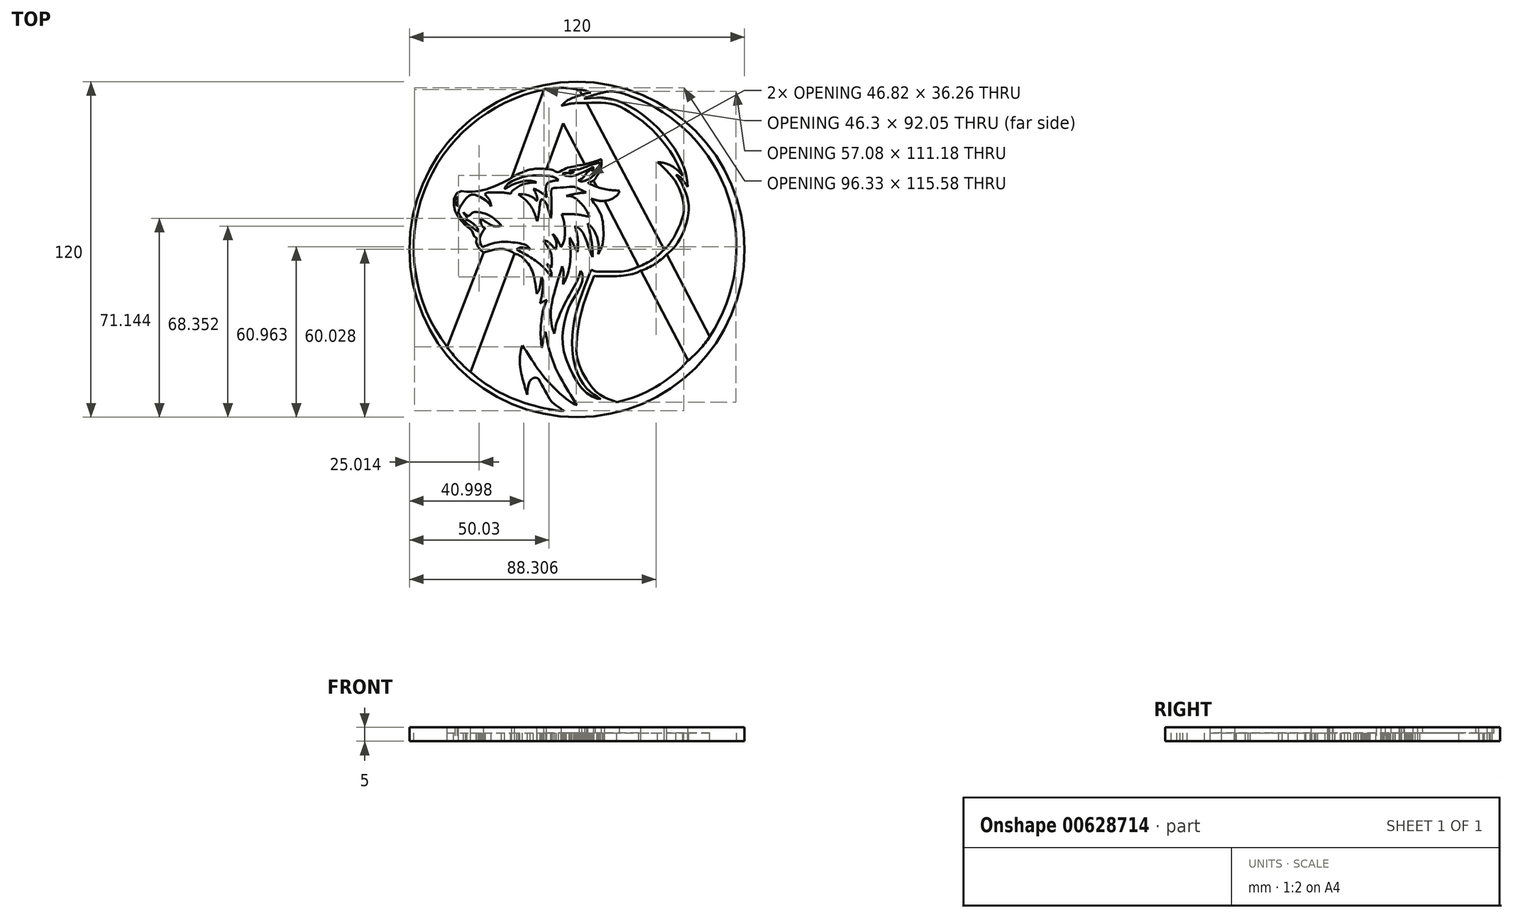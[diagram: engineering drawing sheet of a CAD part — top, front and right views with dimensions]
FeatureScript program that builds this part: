
annotation { "Feature Type Name" : "Feature", "Feature Type Description" : "" }
export const myFeature = defineFeature(function(context is Context, id is Id, definition is map)
    precondition{}
    {
        {
            var Q0;
            Q0=qCreatedBy(makeId("Top.planeOp"),FACE);
            var sketch = newSketch(context, id + "F0", { "sketchPlane" : qUnion([Q0])});
            skCircle(sketch, "E0", {"center": v(0, 0) * mm, "radius": 60 * mm});
            skLineSegment(sketch, "E1", {"start": v(0, 0) * mm, "end": v(60, 0) * mm});
            skSolve(sketch);
        }
        {
            var Q0;
            Q0 = qSketchRegion(id + "F0", true);
            extrude(context, id + "F1", {"entities" : qUnion([Q0]), "depth" : 5 * mm, "offsetDistance" : 25 * mm});
        }
        {
            var Q0;
            Q0=makeQuery(id+"F1.opExtrude","CAP_FACE",FACE,{"disambiguationData":[OSD([sQuery(id+"F0.wireOp",EDGE,"E0")])],"isStart":false});
            var sketch = newSketch(context, id + "F2", { "sketchPlane" : qUnion([Q0])});
            skLineSegment(sketch, "E2", {"start": v(-46.49, -34.88) * mm, "end": v(-33.38, -1.05) * mm});
            skFitSpline(sketch, "E3", {"points": [v(-33.38, -1.05) * mm, v(-34.17, -0.52) * mm, v(-35.37, 0.87) * mm, v(-36.07, 2.59) * mm, v(-35.97, 4.21) * mm, v(-36.9, 4.86) * mm, v(-37.83, 7.18) * mm, v(-38.3, 7.46) * mm, v(-40.7, 9.4) * mm, v(-42.79, 12.05) * mm, v(-43.86, 14.6) * mm, v(-44.04, 17.94) * mm, v(-42.51, 20.62) * mm, v(-40.29, 20.72) * mm, v(-37.46, 20.62) * mm, v(-32.91, 21.37) * mm, v(-26.4, 23.96) * mm, v(-23.59, 25.51) * mm, v(-23.4, 25.77) * mm], "startDerivative": vector(-21.56, 12.24) * mm, "endDerivative": vector(5.42, 11.23) * mm});
            skLineSegment(sketch, "E4", {"start": v(-23.4, 25.77) * mm, "end": v(-11.84, 57.17) * mm});
            skArc(sketch, "E5", {"start": v(-11.84, 57.17) * mm, "mid": v(-54.75, 20.77) * mm, "end": v(-46.49, -34.88) * mm});
            skLineSegment(sketch, "E6", {"start": v(-10.87, 28.8) * mm, "end": v(-4.96, 45.18) * mm});
            skLineSegment(sketch, "E7", {"start": v(-4.96, 45.18) * mm, "end": v(2.82, 30.48) * mm});
            skFitSpline(sketch, "E8", {"points": [v(2.82, 30.48) * mm, v(-0.57, 29.84) * mm, v(-4.3, 28.83) * mm, v(-6.98, 27.68) * mm, v(-8.34, 28.31) * mm, v(-10.87, 28.8) * mm], "startDerivative": vector(-14.97, -2.9) * mm, "endDerivative": vector(-14.54, 1.3) * mm});
            skLineSegment(sketch, "E9", {"start": v(0.84, 57.1) * mm, "end": v(1.79, 55.35) * mm});
            skFitSpline(sketch, "E10", {"points": [v(1.79, 55.35) * mm, v(2.86, 55.77) * mm, v(4.94, 56.14) * mm], "startDerivative": vector(2.3, 1.07) * mm, "endDerivative": vector(3.92, 0.54) * mm});
            skFitSpline(sketch, "E11", {"points": [v(4.94, 56.14) * mm, v(2.72, 56.93) * mm, v(0.84, 57.1) * mm], "startDerivative": vector(-4.26, 1.8) * mm, "endDerivative": vector(-3.93, 0.1) * mm});
            skLineSegment(sketch, "E12", {"start": v(-38.15, -43.82) * mm, "end": v(-22.3, -1.52) * mm});
            skFitSpline(sketch, "E13", {"points": [v(-22.3, -1.52) * mm, v(-20.22, -2.35) * mm, v(-18, -4.48) * mm, v(-16.37, -6.87) * mm, v(-15.08, -11.26) * mm, v(-14.4, -15.69) * mm, v(-14.4, -15.87) * mm], "startDerivative": vector(13.58, -3.84) * mm, "endDerivative": vector(0, -2.59) * mm});
            skFitSpline(sketch, "E14", {"points": [v(-14.4, -15.87) * mm, v(-13.67, -14.7) * mm, v(-13.09, -12.52) * mm, v(-12.7, -9.86) * mm], "startDerivative": vector(2.88, 3.88) * mm, "endDerivative": vector(0.92, 7.04) * mm});
            skFitSpline(sketch, "E15", {"points": [v(-12.7, -9.86) * mm, v(-12.2, -11.16) * mm, v(-12.39, -15.28) * mm, v(-13.2, -19.27) * mm], "startDerivative": vector(2.62, -4.79) * mm, "endDerivative": vector(-2.31, -9.85) * mm});
            skFitSpline(sketch, "E16", {"points": [v(-13.2, -19.27) * mm, v(-12.2, -18.7) * mm, v(-10.79, -18.09) * mm], "startDerivative": vector(2.05, 1.23) * mm, "endDerivative": vector(2.75, 1.13) * mm});
            skFitSpline(sketch, "E17", {"points": [v(-10.79, -18.09) * mm, v(-11.98, -21.3) * mm, v(-12.7, -25.28) * mm, v(-13.04, -30.32) * mm, v(-12.6, -35.24) * mm], "startDerivative": vector(-5.92, -14.1) * mm, "endDerivative": vector(2.31, -18.23) * mm});
            skFitSpline(sketch, "E18", {"points": [v(-12.6, -35.24) * mm, v(-11.92, -31.87) * mm, v(-11.18, -29.5) * mm], "startDerivative": vector(1.15, 6.53) * mm, "endDerivative": vector(1.7, 4.92) * mm});
            skFitSpline(sketch, "E19", {"points": [v(-11.18, -29.5) * mm, v(-10.32, -34.2) * mm, v(-9.13, -38.45) * mm, v(-7.5, -42.78) * mm, v(-4.05, -49.14) * mm, v(0, -55.7) * mm], "startDerivative": vector(4.16, -25.97) * mm, "endDerivative": vector(17.44, -27.8) * mm});
            skFitSpline(sketch, "E20", {"points": [v(0, -55.7) * mm, v(-2.24, -54.63) * mm, v(-6.84, -50.89) * mm, v(-12.8, -44.36) * mm, v(-16.52, -38.89) * mm, v(-19.53, -34.4) * mm], "startDerivative": vector(-15.9, 6.3) * mm, "endDerivative": vector(-15.34, 22.51) * mm});
            skFitSpline(sketch, "E21", {"points": [v(-19.53, -34.4) * mm, v(-20.18, -36.36) * mm, v(-20.45, -41.1) * mm, v(-19.79, -45.08) * mm, v(-18.66, -49.13) * mm, v(-17.8, -52.06) * mm], "startDerivative": vector(-4.69, -11.1) * mm, "endDerivative": vector(4.51, -15) * mm});
            skFitSpline(sketch, "E22", {"points": [v(-17.8, -52.06) * mm, v(-17.61, -49.34) * mm, v(-16.89, -47.25) * mm, v(-15.77, -46.14) * mm, v(-14.8, -45.9) * mm, v(-14, -46.11) * mm, v(-12.82, -48.04) * mm, v(-10.65, -51.85) * mm, v(-8.9, -54.58) * mm, v(-4.64, -57.76) * mm, v(-4.64, -57.76) * mm], "startDerivative": vector(0.44, 23.71) * mm, "endDerivative": vector(-0.04, -0.37) * mm});
            skFitSpline(sketch, "E23", {"points": [v(-4.64, -57.76) * mm, v(-6.58, -57.76) * mm, v(-9.98, -57.16) * mm, v(-15.93, -55.78) * mm, v(-23.66, -53.1) * mm, v(-26.4, -51.82) * mm, v(-32.93, -47.92) * mm, v(-38.15, -43.82) * mm], "startDerivative": vector(-20.53, -1.09) * mm, "endDerivative": vector(-28.95, 24.63) * mm});
            skFitSpline(sketch, "E24", {"points": [v(1.34, -7.66) * mm, v(1.89, -8.56) * mm, v(1.98, -10.4) * mm, v(1.29, -13.28) * mm, v(-1.4, -17.85) * mm, v(-3.38, -22.03) * mm, v(-4.93, -28.7) * mm, v(-4.83, -35.75) * mm, v(-1.91, -43.87) * mm, v(2.1, -50.06) * mm, v(6.63, -53.19) * mm, v(8.56, -53.57) * mm], "startDerivative": vector(14.5, -18.02) * mm, "endDerivative": vector(28.92, -2.36) * mm});
            skFitSpline(sketch, "E25", {"points": [v(8.56, -53.57) * mm, v(6.73, -52.4) * mm, v(4.6, -50.75) * mm, v(2.55, -48.53) * mm, v(0.37, -44.86) * mm, v(-0.72, -41.8) * mm, v(-1.7, -35.87) * mm, v(-1.52, -29.5) * mm, v(-0.5, -23.24) * mm, v(1.28, -17.24) * mm, v(3.74, -10.65) * mm, v(5.12, -7.31) * mm, v(5.12, -7.31) * mm], "startDerivative": vector(-28.43, 17.64) * mm, "endDerivative": vector(0.41, 0.2) * mm});
            skFitSpline(sketch, "E26", {"points": [v(5.12, -7.31) * mm, v(7.08, -7.87) * mm, v(12.4, -7.96) * mm, v(17.2, -7.75) * mm, v(22.17, -6.17) * mm], "startDerivative": vector(9.64, -3.8) * mm, "endDerivative": vector(18.04, 7.02) * mm});
            skLineSegment(sketch, "E27", {"start": v(22.17, -6.17) * mm, "end": v(9.86, 17.38) * mm});
            skFitSpline(sketch, "E28", {"points": [v(9.86, 17.38) * mm, v(8.16, 17.38) * mm, v(5.05, 18.15) * mm], "startDerivative": vector(-3.75, -0.28) * mm, "endDerivative": vector(-5.77, 1.7) * mm});
            skFitSpline(sketch, "E29", {"points": [v(5.05, 18.15) * mm, v(5.63, 17.24) * mm, v(8.02, 13.66) * mm, v(9.13, 10.5) * mm, v(9.47, 6.96) * mm, v(9.14, 1.8) * mm, v(7.6, -1.65) * mm], "startDerivative": vector(4.69, -7.98) * mm, "endDerivative": vector(-10.37, -17.94) * mm});
            skFitSpline(sketch, "E30", {"points": [v(7.6, -1.65) * mm, v(7.8, 0.11) * mm, v(7.49, 3.13) * mm, v(6.25, 6.49) * mm, v(4.82, 8.42) * mm, v(3.82, 9.31) * mm], "startDerivative": vector(1.7, 9.49) * mm, "endDerivative": vector(-6.48, 5.26) * mm});
            skFitSpline(sketch, "E31", {"points": [v(3.82, 9.31) * mm, v(4.27, 7.86) * mm, v(5.16, 3.44) * mm, v(5.6, -0.82) * mm, v(5.55, -2.7) * mm], "startDerivative": vector(2.36, -6.84) * mm, "endDerivative": vector(-0.55, -8.47) * mm});
            skFitSpline(sketch, "E32", {"points": [v(5.55, -2.7) * mm, v(4.58, -0.32) * mm, v(3.43, 3) * mm, v(2, 6.15) * mm, v(0.4, 7.82) * mm, v(-0.65, 8.4) * mm], "startDerivative": vector(-4.82, 11.32) * mm, "endDerivative": vector(-7.3, 3.5) * mm});
            skFitSpline(sketch, "E33", {"points": [v(-0.65, 8.4) * mm, v(-0.19, 6.31) * mm, v(0.34, 3.16) * mm, v(0.3, 0.22) * mm, v(0.15, -1) * mm], "startDerivative": vector(1.83, -8.24) * mm, "endDerivative": vector(-0.92, -5.9) * mm});
            skFitSpline(sketch, "E34", {"points": [v(0.15, -1) * mm, v(-0.5, 0.18) * mm, v(-1.47, 2.17) * mm, v(-2.6, 4.28) * mm], "startDerivative": vector(-2.33, 3.92) * mm, "endDerivative": vector(-3.13, 5.64) * mm});
            skFitSpline(sketch, "E35", {"points": [v(-2.6, 4.28) * mm, v(-2.46, 1.79) * mm, v(-2.34, -3.15) * mm, v(-3.46, -9.06) * mm, v(-4.97, -12.54) * mm], "startDerivative": vector(0.59, -11.93) * mm, "endDerivative": vector(-6.71, -13.43) * mm});
            skFitSpline(sketch, "E36", {"points": [v(-4.97, -12.54) * mm, v(-4.83, -10.25) * mm, v(-4.83, -8) * mm, v(-5.3, -6.02) * mm], "startDerivative": vector(0.43, 6.67) * mm, "endDerivative": vector(-1.83, 6) * mm});
            skFitSpline(sketch, "E37", {"points": [v(-5.3, -6.02) * mm, v(-5.97, -8.23) * mm, v(-7.65, -13.86) * mm, v(-8.87, -18.65) * mm, v(-9.38, -22.52) * mm, v(-9.11, -26.8) * mm, v(-8.1, -30.2) * mm], "startDerivative": vector(-4.59, -15.27) * mm, "endDerivative": vector(7.54, -20.96) * mm});
            skFitSpline(sketch, "E38", {"points": [v(-8.1, -30.2) * mm, v(-7.43, -26.81) * mm, v(-5.58, -21.9) * mm, v(-2.94, -16.7) * mm, v(-0.85, -13.01) * mm, v(0.66, -9.79) * mm, v(1.34, -7.66) * mm], "startDerivative": vector(3.24, 21.07) * mm, "endDerivative": vector(4.62, 16.25) * mm});
            skFitSpline(sketch, "E39", {"points": [v(31.26, 0) * mm, v(34.04, 3.29) * mm, v(37.22, 9.75) * mm, v(38.22, 15.62) * mm, v(36.23, 22.58) * mm, v(32.65, 27.65) * mm, v(28.87, 31.18) * mm], "startDerivative": vector(19.68, 20.28) * mm, "endDerivative": vector(-24.78, 21.54) * mm});
            skFitSpline(sketch, "E40", {"points": [v(28.87, 31.18) * mm, v(30.68, 31.05) * mm, v(33.64, 29.98) * mm, v(36.21, 28.16) * mm, v(37.87, 26.33) * mm], "startDerivative": vector(8.16, 0.03) * mm, "endDerivative": vector(6.3, -7.66) * mm});
            skFitSpline(sketch, "E41", {"points": [v(37.87, 26.33) * mm, v(34.98, 32.47) * mm, v(27.72, 42.09) * mm, v(21.1, 47.56) * mm, v(14.87, 51.28) * mm, v(9.32, 52.5) * mm, v(3.38, 52.38) * mm], "startDerivative": vector(-14.7, 36.43) * mm, "endDerivative": vector(-40.77, -2.44) * mm});
            skLineSegment(sketch, "E42", {"start": v(3.38, 52.38) * mm, "end": v(31.26, 0) * mm});
            skFitSpline(sketch, "E43", {"points": [v(32.1, -1.72) * mm, v(34.65, 0.58) * mm, v(37.67, 5.34) * mm, v(39.86, 12.73) * mm, v(39.47, 18.64) * mm, v(36.77, 24.9) * mm, v(35.4, 26.72) * mm], "startDerivative": vector(18.8, 15.01) * mm, "endDerivative": vector(-11.44, 13.12) * mm});
            skFitSpline(sketch, "E44", {"points": [v(35.4, 26.72) * mm, v(37.01, 25.85) * mm, v(39.58, 22.4) * mm], "startDerivative": vector(4.06, -1.53) * mm, "endDerivative": vector(4.3, -6.75) * mm});
            skFitSpline(sketch, "E45", {"points": [v(39.58, 22.4) * mm, v(39.16, 26.48) * mm, v(36.77, 32.91) * mm, v(31.7, 40.47) * mm, v(26.42, 45.83) * mm, v(18.62, 51.34) * mm, v(10.27, 54.23) * mm, v(2.54, 53.88) * mm], "startDerivative": vector(-1.66, 37) * mm, "endDerivative": vector(-53.18, -6.81) * mm});
            skFitSpline(sketch, "E46", {"points": [v(2.54, 53.88) * mm, v(4.93, 54.92) * mm, v(9.15, 56.12) * mm], "startDerivative": vector(5.07, 2.46) * mm, "endDerivative": vector(8.02, 2.04) * mm});
            skFitSpline(sketch, "E47", {"points": [v(9.15, 56.12) * mm, v(11.4, 56.52) * mm, v(14.67, 56.3) * mm, v(18.96, 54.98) * mm], "startDerivative": vector(7.73, 1.8) * mm, "endDerivative": vector(11.22, -4) * mm});
            skArc(sketch, "E48", {"start": v(47.53, -31.22) * mm, "mid": v(54.17, 18.81) * mm, "end": v(18.96, 54.98) * mm});
            skLineSegment(sketch, "E49", {"start": v(47.53, -31.22) * mm, "end": v(32.1, -1.72) * mm});
            skLineSegment(sketch, "E50", {"start": v(22.84, -7.6) * mm, "end": v(39.82, -39.7) * mm});
            skFitSpline(sketch, "E51", {"points": [v(22.84, -7.6) * mm, v(19.85, -8.8) * mm, v(12.97, -9.6) * mm, v(6.1, -9.5) * mm], "startDerivative": vector(-10.27, -5.18) * mm, "endDerivative": vector(-17.93, 0.7) * mm});
            skFitSpline(sketch, "E52", {"points": [v(6.1, -9.5) * mm, v(4, -14.83) * mm, v(1.2, -23.88) * mm, v(0, -31.84) * mm, v(0.46, -40.49) * mm, v(6.73, -50.75) * mm, v(10.57, -53.2) * mm, v(14.3, -54.63) * mm], "startDerivative": vector(-15.99, -38.63) * mm, "endDerivative": vector(35.93, -13.2) * mm});
            skArc(sketch, "E53", {"start": v(14.3, -54.63) * mm, "mid": v(28.24, -49.2) * mm, "end": v(39.82, -39.7) * mm});
            skFitSpline(sketch, "E54", {"points": [v(-9.2, -9.78) * mm, v(-13.22, -5.25) * mm, v(-21.57, 0) * mm], "startDerivative": vector(-7.9, 10.5) * mm, "endDerivative": vector(-16.5, 9.1) * mm});
            skFitSpline(sketch, "E55", {"points": [v(-21.57, 0) * mm, v(-20.13, 0.71) * mm, v(-16.7, 0) * mm], "startDerivative": vector(3.13, 2.36) * mm, "endDerivative": vector(6.4, -2.08) * mm});
            skFitSpline(sketch, "E56", {"points": [v(-16.7, 0) * mm, v(-18.44, 1.6) * mm, v(-23.11, 2.55) * mm, v(-27.94, 2.65) * mm, v(-33.9, 0.86) * mm], "startDerivative": vector(-7.61, 9.84) * mm, "endDerivative": vector(-20.74, -7.72) * mm});
            skFitSpline(sketch, "E57", {"points": [v(-33.9, 0.86) * mm, v(-34.8, 3.5) * mm, v(-33.9, 6.13) * mm, v(-32.8, 7.67) * mm], "startDerivative": vector(-3.8, 7.28) * mm, "endDerivative": vector(3.74, 4.76) * mm});
            skFitSpline(sketch, "E58", {"points": [v(-32.8, 7.67) * mm, v(-33.9, 8.32) * mm, v(-34.4, 9.76) * mm, v(-34.45, 11.15) * mm], "startDerivative": vector(-3.87, 1.5) * mm, "endDerivative": vector(0.05, 4.05) * mm});
            skFitSpline(sketch, "E59", {"points": [v(-34.45, 11.15) * mm, v(-32.8, 9.96) * mm, v(-30.67, 8.72) * mm, v(-29.33, 8.27) * mm, v(-27, 8.47) * mm], "startDerivative": vector(6.14, -4.73) * mm, "endDerivative": vector(9.51, 1.44) * mm});
            skFitSpline(sketch, "E60", {"points": [v(-27, 8.47) * mm, v(-28.78, 10.3) * mm, v(-32.26, 12.6) * mm, v(-35.24, 13.34) * mm, v(-37.13, 13.3) * mm, v(-38.38, 12.25) * mm, v(-39.17, 12.1) * mm, v(-40.66, 13.24) * mm], "startDerivative": vector(-10.12, 11.46) * mm, "endDerivative": vector(-11.9, 11.25) * mm});
            skFitSpline(sketch, "E61", {"points": [v(-40.66, 13.24) * mm, v(-39.9, 12.1) * mm, v(-39.4, 11.47) * mm, v(-39.88, 10.7) * mm], "startDerivative": vector(1.84, -3.2) * mm, "endDerivative": vector(-2.34, -2.57) * mm});
            skFitSpline(sketch, "E62", {"points": [v(-39.88, 10.7) * mm, v(-38.96, 10.38) * mm, v(-36.86, 9) * mm, v(-35.66, 7.67) * mm, v(-35.26, 6.46) * mm], "startDerivative": vector(4.18, -1.1) * mm, "endDerivative": vector(1.3, -5.52) * mm});
            skFitSpline(sketch, "E63", {"points": [v(-35.26, 6.46) * mm, v(-36.84, 7.39) * mm, v(-39.17, 9.13) * mm, v(-41.4, 11.45) * mm, v(-42.44, 13.5) * mm, v(-41.53, 15.61) * mm, v(-39.88, 18.04) * mm, v(-38.3, 19.4) * mm, v(-36.6, 19.57) * mm, v(-34.45, 18.7) * mm, v(-32.44, 17.44) * mm, v(-31.25, 16.14) * mm, v(-30.76, 15.44) * mm], "startDerivative": vector(-19.73, 11.03) * mm, "endDerivative": vector(8.3, -12.4) * mm});
            skFitSpline(sketch, "E64", {"points": [v(-30.76, 15.44) * mm, v(-30.9, 16.58) * mm, v(-31.75, 18.3) * mm, v(-32.97, 19.7) * mm], "startDerivative": vector(-0.17, 3.87) * mm, "endDerivative": vector(-3.6, 3.66) * mm});
            skFitSpline(sketch, "E65", {"points": [v(-32.97, 19.7) * mm, v(-32.37, 20.2) * mm, v(-29.75, 20.44) * mm, v(-26.51, 20.38) * mm, v(-23.76, 19.94) * mm], "startDerivative": vector(3.07, 3.83) * mm, "endDerivative": vector(9.66, -1.93) * mm});
            skFitSpline(sketch, "E66", {"points": [v(-23.76, 19.94) * mm, v(-23.27, 20.89) * mm, v(-21.35, 22.27) * mm, v(-18.44, 23.57) * mm, v(-14.49, 24) * mm, v(-14.49, 24) * mm], "startDerivative": vector(2.02, 5.85) * mm, "endDerivative": vector(-0.05, 0.18) * mm});
            skFitSpline(sketch, "E67", {"points": [v(-14.49, 24) * mm, v(-15.49, 24.42) * mm, v(-18.83, 24.46) * mm, v(-22.88, 23.24) * mm, v(-24.92, 22.1) * mm, v(-25.75, 21.62) * mm, v(-25.83, 22) * mm, v(-24.8, 23.33) * mm, v(-21.25, 25.34) * mm, v(-16.25, 26.47) * mm, v(-12.37, 26.44) * mm, v(-9.95, 26.34) * mm, v(-7.83, 25.73) * mm, v(-6.54, 24.78) * mm], "startDerivative": vector(-16.04, 8.88) * mm, "endDerivative": vector(18.42, -16.07) * mm});
            skFitSpline(sketch, "E68", {"points": [v(-6.54, 24.78) * mm, v(-8.55, 24.53) * mm, v(-10.46, 23.76) * mm, v(-11.14, 21.91) * mm, v(-10.77, 18.59) * mm], "startDerivative": vector(-8.44, -0.8) * mm, "endDerivative": vector(2.08, -11.65) * mm});
            skFitSpline(sketch, "E69", {"points": [v(-10.77, 18.59) * mm, v(-12.34, 20.06) * mm, v(-14.83, 21.46) * mm, v(-15.63, 21.7) * mm], "startDerivative": vector(-3.74, 4.08) * mm, "endDerivative": vector(-3, 0.69) * mm});
            skFitSpline(sketch, "E70", {"points": [v(-15.63, 21.7) * mm, v(-14.84, 20.25) * mm, v(-14.22, 18.59) * mm, v(-14.37, 17.45) * mm, v(-15.5, 18.38) * mm, v(-17.57, 19.45) * mm, v(-19.36, 19.78) * mm, v(-20.96, 19.7) * mm], "startDerivative": vector(5.6, -10.11) * mm, "endDerivative": vector(-11.36, -1.2) * mm});
            skFitSpline(sketch, "E71", {"points": [v(-20.96, 19.7) * mm, v(-19.45, 18.59) * mm, v(-17.17, 16.39) * mm, v(-15.38, 13.42) * mm, v(-14.27, 10.16) * mm], "startDerivative": vector(7.17, -5) * mm, "endDerivative": vector(3.61, -12.23) * mm});
            skFitSpline(sketch, "E72", {"points": [v(-14.27, 10.16) * mm, v(-13.9, 11.58) * mm, v(-13.41, 14.9) * mm, v(-13.14, 16.87) * mm, v(-12.67, 17.94) * mm, v(-11.45, 17.12) * mm, v(-9.96, 13.54) * mm, v(-9.45, 11.26) * mm], "startDerivative": vector(3.19, 10.27) * mm, "endDerivative": vector(2.68, -13.95) * mm});
            skFitSpline(sketch, "E73", {"points": [v(-9.45, 11.26) * mm, v(-9.11, 12.82) * mm, v(-9.14, 16.76) * mm, v(-9.21, 20.81) * mm, v(-8.95, 21.72) * mm, v(-6.5, 22.1) * mm, v(-2.65, 22.38) * mm, v(-1.01, 22.38) * mm, v(3.3, 20.38) * mm], "startDerivative": vector(4.25, 14.55) * mm, "endDerivative": vector(29.84, -16) * mm});
            skFitSpline(sketch, "E74", {"points": [v(3.3, 20.38) * mm, v(1.3, 20.2) * mm, v(-1.65, 19.7) * mm, v(-3.78, 19.12) * mm], "startDerivative": vector(-6.15, -0.37) * mm, "endDerivative": vector(-6.25, -1.83) * mm});
            skFitSpline(sketch, "E75", {"points": [v(-3.78, 19.12) * mm, v(-1.49, 18.83) * mm, v(1.57, 16.38) * mm, v(3.64, 13.54) * mm, v(4.4, 11.66) * mm], "startDerivative": vector(10.1, 0.22) * mm, "endDerivative": vector(2.98, -8.67) * mm});
            skFitSpline(sketch, "E76", {"points": [v(4.4, 11.66) * mm, v(1.58, 12.27) * mm, v(-2.02, 12.66) * mm, v(-5.48, 12.6) * mm], "startDerivative": vector(-8.75, 2.07) * mm, "endDerivative": vector(-10.03, -0.47) * mm});
            skFitSpline(sketch, "E77", {"points": [v(-5.48, 12.6) * mm, v(-4.63, 9.7) * mm, v(-4.48, 3.8) * mm, v(-5.66, 0.84) * mm], "startDerivative": vector(3.24, -8.58) * mm, "endDerivative": vector(-4.79, -8.48) * mm});
            skFitSpline(sketch, "E78", {"points": [v(-9.2, -9.78) * mm, v(-9.07, -9.08) * mm, v(-9.6, -7.2) * mm, v(-10.77, -5.3) * mm], "startDerivative": vector(0.85, 2.7) * mm, "endDerivative": vector(-3.21, 4.5) * mm});
            skFitSpline(sketch, "E79", {"points": [v(-10.77, -5.3) * mm, v(-10.36, -5.42) * mm, v(-9.57, -6) * mm, v(-9.2, -6.52) * mm], "startDerivative": vector(1.39, -0.23) * mm, "endDerivative": vector(0.93, -1.53) * mm});
            skFitSpline(sketch, "E80", {"points": [v(-9.2, -6.52) * mm, v(-8.98, -4.53) * mm, v(-9.36, -1.17) * mm, v(-10.58, 1.13) * mm, v(-12.04, 3.13) * mm], "startDerivative": vector(1.31, 8.28) * mm, "endDerivative": vector(-6.08, 8.16) * mm});
            skFitSpline(sketch, "E81", {"points": [v(-12.04, 3.13) * mm, v(-10.63, 2.89) * mm, v(-8.77, 1.2) * mm, v(-7.54, 0) * mm], "startDerivative": vector(4.75, 0.01) * mm, "endDerivative": vector(3.6, -3.35) * mm});
            skFitSpline(sketch, "E82", {"points": [v(-7.54, 0) * mm, v(-7.36, 1.92) * mm, v(-7.7, 3.57) * mm, v(-8.73, 5.5) * mm], "startDerivative": vector(0.85, 5.9) * mm, "endDerivative": vector(-3.33, 5.51) * mm});
            skFitSpline(sketch, "E83", {"points": [v(-8.73, 5.5) * mm, v(-7.73, 4.57) * mm, v(-6.54, 2.59) * mm, v(-5.66, 0.84) * mm], "startDerivative": vector(3.53, -2.76) * mm, "endDerivative": vector(2.4, -4.9) * mm});
            skFitSpline(sketch, "E84", {"points": [v(0.44, 24.78) * mm, v(1.35, 24.32) * mm, v(3.56, 24.89) * mm, v(5.95, 26.42) * mm, v(7.67, 28.88) * mm, v(8.13, 30.34) * mm, v(8.15, 31.22) * mm], "startDerivative": vector(6.33, -4.98) * mm, "endDerivative": vector(-0.25, 7.3) * mm});
            skFitSpline(sketch, "E85", {"points": [v(8.15, 31.22) * mm, v(6.62, 30.73) * mm, v(3.57, 29.7) * mm, v(0.7, 28.72) * mm, v(-1.16, 28.4) * mm, v(-2.77, 28.17) * mm], "startDerivative": vector(-8.2, -2.6) * mm, "endDerivative": vector(-9.34, -1.47) * mm});
            skFitSpline(sketch, "E86", {"points": [v(-2.77, 28.17) * mm, v(-2.48, 27.95) * mm, v(-1.59, 27.93) * mm, v(-1.1, 27.8) * mm], "startDerivative": vector(0.8, -1.02) * mm, "endDerivative": vector(1.31, -0.58) * mm});
            skFitSpline(sketch, "E87", {"points": [v(-1.1, 27.8) * mm, v(-1.53, 27.4) * mm, v(-3.11, 27.34) * mm, v(-4.44, 27.4) * mm, v(-5.22, 27.1) * mm], "startDerivative": vector(-1.7, -2.48) * mm, "endDerivative": vector(-3.3, -1.65) * mm});
            skFitSpline(sketch, "E88", {"points": [v(-5.22, 27.1) * mm, v(-4.72, 26.64) * mm, v(-2.77, 26.26) * mm, v(-0.34, 26.6) * mm, v(2.1, 27.68) * mm, v(4.6, 28.8) * mm, v(5.75, 29.54) * mm, v(5.93, 29.1) * mm, v(5.6, 28.17) * mm, v(5.3, 28.37) * mm, v(5.2, 28.6) * mm, v(4.4, 28.26) * mm, v(3.48, 27.36) * mm, v(2.44, 26.04) * mm, v(1.4, 25.13) * mm, v(0.44, 24.78) * mm], "startDerivative": vector(7.66, -9.88) * mm, "endDerivative": vector(-16, -4.19) * mm});
            skFitSpline(sketch, "E89", {"points": [v(-42.53, 15.94) * mm, v(-42.87, 17.53) * mm, v(-42.8, 18.79) * mm, v(-43.46, 18.11) * mm, v(-43.6, 16.99) * mm, v(-43.27, 16.14) * mm, v(-42.56, 15.58) * mm, v(-42.53, 15.94) * mm]});
            skSolve(sketch);
        }
        {
            var Q0;
            Q0 = qSketchRegion(id + "F2", true);
            extrude(context, id + "F3", {"entities" : qUnion([Q0]), "operationType" : NewBodyOperationType.REMOVE, "endBound" : BoundingType.THROUGH_ALL, "oppositeDirection" : true, "depth" : 25 * mm, "offsetDistance" : 25 * mm});
        }
        {
            var Q0;
            Q0=makeQuery(id+"F1.opExtrude","CAP_FACE",FACE,{"disambiguationData":[OSD([sQuery(id+"F0.wireOp",EDGE,"E0")])],"isStart":false});
            var sketch = newSketch(context, id + "F4", { "sketchPlane" : qUnion([Q0])});
            skFitSpline(sketch, "E90", {"points": [v(-23.4, 25.77) * mm, v(-19.25, 27.75) * mm, v(-15.4, 28.8) * mm, v(-10.87, 28.8) * mm], "startDerivative": vector(12.23, 6.28) * mm, "endDerivative": vector(13.7, -0.73) * mm});
            skLineSegment(sketch, "E91", {"start": v(-10.87, 28.8) * mm, "end": v(-4.96, 45.18) * mm});
            skLineSegment(sketch, "E92", {"start": v(-4.96, 45.18) * mm, "end": v(2.82, 30.48) * mm});
            skFitSpline(sketch, "E93", {"points": [v(2.82, 30.48) * mm, v(4.75, 30.96) * mm, v(8.75, 32.25) * mm], "startDerivative": vector(4.31, 0.98) * mm, "endDerivative": vector(7.36, 2.46) * mm});
            skFitSpline(sketch, "E94", {"points": [v(8.75, 32.25) * mm, v(8.75, 30.74) * mm, v(8.25, 28.26) * mm, v(6.64, 25.52) * mm], "startDerivative": vector(0.19, -5.28) * mm, "endDerivative": vector(-4.83, -6.9) * mm});
            skLineSegment(sketch, "E95", {"start": v(39.82, -39.7) * mm, "end": v(22.84, -7.6) * mm});
            skArc(sketch, "E96", {"start": v(22.84, -7.6) * mm, "mid": v(27.84, -5.24) * mm, "end": v(32.1, -1.72) * mm});
            skLineSegment(sketch, "E97", {"start": v(32.1, -1.72) * mm, "end": v(47.53, -31.22) * mm});
            skArc(sketch, "E98", {"start": v(39.82, -39.7) * mm, "mid": v(44, -35.76) * mm, "end": v(47.53, -31.22) * mm});
            skFitSpline(sketch, "E99", {"points": [v(6.64, 25.52) * mm, v(6.37, 25.1) * mm, v(6.02, 24.74) * mm], "startDerivative": vector(-0.5, -0.89) * mm, "endDerivative": vector(-0.73, -0.68) * mm});
            skArc(sketch, "E100", {"start": v(22.17, -6.17) * mm, "mid": v(27.05, -3.58) * mm, "end": v(31.26, 0) * mm});
            skLineSegment(sketch, "E101", {"start": v(3.38, 52.38) * mm, "end": v(31.26, 0) * mm});
            skFitSpline(sketch, "E102", {"points": [v(3.38, 52.38) * mm, v(1.07, 52.38) * mm, v(-2.11, 52.2) * mm, v(-5.57, 51.33) * mm], "startDerivative": vector(-7.57, 0.01) * mm, "endDerivative": vector(-9.48, -2.9) * mm});
            skFitSpline(sketch, "E103", {"points": [v(-5.57, 51.33) * mm, v(-3.61, 53.19) * mm, v(0.53, 54.98) * mm, v(1.79, 55.35) * mm], "startDerivative": vector(4.63, 5.7) * mm, "endDerivative": vector(4.39, 1.15) * mm});
            skLineSegment(sketch, "E104", {"start": v(1.79, 55.35) * mm, "end": v(0.84, 57.1) * mm});
            skArc(sketch, "E105", {"start": v(0.84, 57.1) * mm, "mid": v(-5.5, 57.82) * mm, "end": v(-11.84, 57.17) * mm});
            skLineSegment(sketch, "E106", {"start": v(-11.84, 57.17) * mm, "end": v(-23.4, 25.77) * mm});
            skLineSegment(sketch, "E107", {"start": v(-46.49, -34.88) * mm, "end": v(-33.38, -1.05) * mm});
            skFitSpline(sketch, "E108", {"points": [v(-33.38, -1.05) * mm, v(-30.77, -0.35) * mm, v(-27.68, 0.16) * mm, v(-24.76, -0.2) * mm, v(-22.3, -1.52) * mm], "startDerivative": vector(10.5, 2.99) * mm, "endDerivative": vector(9.6, -6.15) * mm});
            skLineSegment(sketch, "E109", {"start": v(-22.3, -1.52) * mm, "end": v(-38.15, -43.82) * mm});
            skArc(sketch, "E110", {"start": v(-46.49, -34.88) * mm, "mid": v(-42.62, -39.63) * mm, "end": v(-38.15, -43.82) * mm});
            skLineSegment(sketch, "E111", {"start": v(22.17, -6.17) * mm, "end": v(9.86, 17.38) * mm});
            skFitSpline(sketch, "E112", {"points": [v(3.98, 23.84) * mm, v(5.02, 24.2) * mm, v(6.02, 24.74) * mm], "startDerivative": vector(2.12, 0.62) * mm, "endDerivative": vector(1.95, 1.16) * mm});
            skFitSpline(sketch, "E113", {"points": [v(3.98, 23.84) * mm, v(5.03, 23.28) * mm, v(9.13, 21.76) * mm, v(15.21, 21.01) * mm], "startDerivative": vector(4.51, -2.6) * mm, "endDerivative": vector(14.18, -0.9) * mm});
            skFitSpline(sketch, "E114", {"points": [v(9.86, 17.38) * mm, v(12.33, 17.99) * mm, v(14.86, 20) * mm, v(15.21, 21.01) * mm], "startDerivative": vector(6.63, 0.8) * mm, "endDerivative": vector(0.6, 4.04) * mm});
            skSolve(sketch);
        }
        {
            var Q0;
            Q0 = qSketchRegion(id + "F4", true);
            extrude(context, id + "F5", {"entities" : qUnion([Q0]), "operationType" : NewBodyOperationType.REMOVE, "oppositeDirection" : true, "depth" : 2 * mm, "offsetDistance" : 25 * mm});
        }
        {
            var Q0;
            Q0=makeQuery(id+"F5.boolean.opBoolean","COPY",FACE,{"derivedFrom":makeQuery(id+"F5.opExtrude","CAP_FACE",FACE,{"disambiguationData":[OSD([sQuery(id+"F4.wireOp",EDGE,"E90"),sQuery(id+"F4.wireOp",EDGE,"E91"),sQuery(id+"F4.wireOp",EDGE,"E92"),sQuery(id+"F4.wireOp",EDGE,"E93"),sQuery(id+"F4.wireOp",EDGE,"E94"),sQuery(id+"F4.wireOp",EDGE,"E99"),sQuery(id+"F4.wireOp",EDGE,"E100"),sQuery(id+"F4.wireOp",EDGE,"E101"),sQuery(id+"F4.wireOp",EDGE,"E102"),sQuery(id+"F4.wireOp",EDGE,"E103"),sQuery(id+"F4.wireOp",EDGE,"E104"),sQuery(id+"F4.wireOp",EDGE,"E105"),sQuery(id+"F4.wireOp",EDGE,"E106"),sQuery(id+"F4.wireOp",EDGE,"E111"),sQuery(id+"F4.wireOp",EDGE,"E112"),sQuery(id+"F4.wireOp",EDGE,"E113"),sQuery(id+"F4.wireOp",EDGE,"E114")])],"isStart":false})});
            var sketch = newSketch(context, id + "F6", { "sketchPlane" : qUnion([Q0])});
            skLineSegment(sketch, "E115", {"start": v(22.17, -6.17) * mm, "end": v(-4.96, 45.18) * mm});
            skFitSpline(sketch, "E116", {"points": [v(3.98, 23.84) * mm, v(4.38, 23.96) * mm, v(4.94, 24.16) * mm, v(5.46, 24.41) * mm, v(5.89, 24.66) * mm], "startDerivative": vector(1.7, 0.5) * mm, "endDerivative": vector(1.7, 1) * mm});
            skFitSpline(sketch, "E117", {"points": [v(3.98, 23.84) * mm, v(4.24, 23.7) * mm, v(4.87, 23.36) * mm, v(5.43, 23.1) * mm, v(6.1, 22.8) * mm, v(7.07, 22.4) * mm], "startDerivative": vector(1.68, -0.97) * mm, "endDerivative": vector(3.98, -1.55) * mm});
            skSolve(sketch);
        }
        {
            var Q0;
            {var subQ0=sQuery(id+"F6.wireOp",EDGE,"E116");var subQ1=makeQuery(id+"F5.boolean.opBoolean","COPY",EDGE,{"derivedFrom":makeQuery(id+"F5.opExtrude","CAP_EDGE",EDGE,{"disambiguationData":[OSD([sQuery(id+"F4.wireOp",EDGE,"E112")])],"isStart":false})});var subQ2=makeQuery(id+"F6.imprint","INTERSECT",VERTEX,{"disambiguationData":[OD(2.0)],"derivedFrom":[subQ1,subQ0]});Q0=makeQuery(id+"F6.imprint","IMPRINT",FACE,{"disambiguationData":[TD([[makeQuery(id+"F6.imprint","IMPRINT",EDGE,{"disambiguationData":[TD([[subQ2,-1.0]])],"derivedFrom":subQ0}),-1.0]])]});}
            var Q1;
            {var subQ0=sQuery(id+"F6.wireOp",EDGE,"E116");var subQ1=makeQuery(id+"F5.boolean.opBoolean","COPY",EDGE,{"derivedFrom":makeQuery(id+"F5.opExtrude","CAP_EDGE",EDGE,{"disambiguationData":[OSD([sQuery(id+"F4.wireOp",EDGE,"E112")])],"isStart":false})});var subQ2=makeQuery(id+"F6.imprint","INTERSECT",VERTEX,{"disambiguationData":[OD(5.0)],"derivedFrom":[subQ1,subQ0]});Q1=makeQuery(id+"F6.imprint","IMPRINT",FACE,{"disambiguationData":[TD([[makeQuery(id+"F6.imprint","IMPRINT",EDGE,{"disambiguationData":[TD([[subQ2,-1.0]])],"derivedFrom":subQ0}),-1.0]])]});}
            var Q2;
            {var subQ0=sQuery(id+"F6.wireOp",EDGE,"E116");var subQ1=makeQuery(id+"F5.boolean.opBoolean","COPY",EDGE,{"derivedFrom":makeQuery(id+"F5.opExtrude","CAP_EDGE",EDGE,{"disambiguationData":[OSD([sQuery(id+"F4.wireOp",EDGE,"E112")])],"isStart":false})});var subQ2=makeQuery(id+"F6.imprint","INTERSECT",VERTEX,{"disambiguationData":[OD(3.0)],"derivedFrom":[subQ1,subQ0]});Q2=makeQuery(id+"F6.imprint","IMPRINT",FACE,{"disambiguationData":[TD([[makeQuery(id+"F6.imprint","IMPRINT",EDGE,{"disambiguationData":[TD([[subQ2,1.0]])],"derivedFrom":subQ0}),-1.0]])]});}
            var Q3;
            {var subQ0=sQuery(id+"F6.wireOp",EDGE,"E116");var subQ1=makeQuery(id+"F5.boolean.opBoolean","COPY",EDGE,{"derivedFrom":makeQuery(id+"F5.opExtrude","CAP_EDGE",EDGE,{"disambiguationData":[OSD([sQuery(id+"F4.wireOp",EDGE,"E112")])],"isStart":false})});var subQ2=makeQuery(id+"F6.imprint","INTERSECT",VERTEX,{"disambiguationData":[OD(0.0)],"derivedFrom":[subQ1,subQ0]});Q3=makeQuery(id+"F6.imprint","IMPRINT",FACE,{"disambiguationData":[TD([[makeQuery(id+"F6.imprint","IMPRINT",EDGE,{"disambiguationData":[TD([[subQ2,1.0]])],"derivedFrom":subQ0}),-1.0]])]});}
            var Q4;
            {var subQ0=sQuery(id+"F6.wireOp",EDGE,"E117");var subQ1=makeQuery(id+"F5.boolean.opBoolean","COPY",EDGE,{"derivedFrom":makeQuery(id+"F5.opExtrude","CAP_EDGE",EDGE,{"disambiguationData":[OSD([sQuery(id+"F4.wireOp",EDGE,"E113")])],"isStart":false})});var subQ3=makeQuery(id+"F6.imprint","INTERSECT",VERTEX,{"disambiguationData":[OD(2.0)],"derivedFrom":[subQ1,subQ0]});Q4=makeQuery(id+"F6.imprint","IMPRINT",FACE,{"disambiguationData":[TD([[makeQuery(id+"F6.imprint","IMPRINT",EDGE,{"disambiguationData":[TD([[subQ3,1.0]])],"derivedFrom":subQ0}),1.0]])]});}
            var Q5;
            {var subQ0=sQuery(id+"F6.wireOp",EDGE,"E117");var subQ1=makeQuery(id+"F5.boolean.opBoolean","COPY",EDGE,{"derivedFrom":makeQuery(id+"F5.opExtrude","CAP_EDGE",EDGE,{"disambiguationData":[OSD([sQuery(id+"F4.wireOp",EDGE,"E113")])],"isStart":false})});var subQ2=makeQuery(id+"F6.imprint","INTERSECT",VERTEX,{"disambiguationData":[OD(0.0)],"derivedFrom":[subQ1,subQ0]});Q5=makeQuery(id+"F6.imprint","IMPRINT",FACE,{"disambiguationData":[TD([[makeQuery(id+"F6.imprint","IMPRINT",EDGE,{"disambiguationData":[TD([[subQ2,1.0]])],"derivedFrom":subQ0}),1.0]])]});}
            var Q6;
            {var subQ0=sQuery(id+"F6.wireOp",EDGE,"E117");var subQ1=makeQuery(id+"F5.boolean.opBoolean","COPY",EDGE,{"derivedFrom":makeQuery(id+"F5.opExtrude","CAP_EDGE",EDGE,{"disambiguationData":[OSD([sQuery(id+"F4.wireOp",EDGE,"E113")])],"isStart":false})});var subQ2=makeQuery(id+"F6.imprint","INTERSECT",VERTEX,{"disambiguationData":[OD(1.0)],"derivedFrom":[subQ1,subQ0]});Q6=makeQuery(id+"F6.imprint","IMPRINT",FACE,{"disambiguationData":[TD([[makeQuery(id+"F6.imprint","IMPRINT",EDGE,{"disambiguationData":[TD([[subQ2,-1.0]])],"derivedFrom":subQ0}),1.0]])]});}
            var Q7;
            {var subQ0=sQuery(id+"F6.wireOp",EDGE,"E116");var subQ18=makeQuery(id+"F6.imprint","IMPRINT",VERTEX,{"disambiguationData":[OD(0.0)],"derivedFrom":subQ0});Q7=makeQuery(id+"F6.imprint","IMPRINT",FACE,{"disambiguationData":[TD([[makeQuery(id+"F6.imprint","IMPRINT",EDGE,{"disambiguationData":[TD([[subQ18,1.0]])],"derivedFrom":subQ0}),-1.0]])]});}
            extrude(context, id + "F7", {"entities" : qUnion([Q0, Q1, Q2, Q3, Q4, Q5, Q6, Q7]), "operationType" : NewBodyOperationType.REMOVE, "endBound" : BoundingType.THROUGH_ALL, "oppositeDirection" : true, "depth" : 25 * mm, "offsetDistance" : 25 * mm});
        }
    });
